# Revit family: DSP_A3-1-External-Lourve-Metal-Door-Full-Louvre-Single
name_source: partatom
category: Doors
revit_build: Autodesk Revit 2016 (Build: 20150220_1215(x64)
units: mm (PartAtom-declared; Revit-internal decimal feet)

## family parameters
Always vertical = Yes
Cut with Voids When Loaded = No
Host = Wall
Room Calculation Point = No
Shared = No

## types (1)
- 914 x 2438mm Louvre
    Cavity Closer Depth = 85 mm  [stored 0.278871 ft]
    Cavity Closer Offset from Ext = 102.5 mm  [stored 0.336286 ft]
    Cavity Closer Width = 50 mm  [stored 0.164042 ft]
    Cill Extension = 25 mm  [stored 0.082021 ft]
    Cill Projection = 30 mm  [stored 0.0984252 ft]
    Cill Thickness = 54.5 mm  [stored 0.178806 ft]
    Construction Type = SF-03
    DONT CHANGE Louvre Length = 722 mm
    Door Panel Height = 2328 mm
    Door Panel Thickness = 44 mm  [stored 0.144357 ft]
    Door Panel Width = 947 mm
    FrameDepth = 89 mm  [stored 0.291995 ft]
    FrameOffset - External = 25 mm  [stored 0.082021 ft]
    FrameWidth = 42 mm  [stored 0.137795 ft]
    Function = Interior
    Handle Style = Handle Domestic (2)
    Handle X Distance = 75 mm  [stored 0.246063 ft]
    Handle Z Distance = 1050 mm  [stored 3.44488 ft]
    Height = 2438 mm
    Keynote = L20
    L Louvre to Handle = 541.5 mm  [stored 1.77657 ft]
    Lower Louvre Height = 300 mm
    Material Door = Metal - Aluminium - Dark
    Material Frame = Metal - Aluminium - Dark
    Material Ironmongery = Door - Handle
    No of Louvres (Lower) = 6
    No of Louvres (Upper) = 44
    O/A Frame Width = 64 mm  [stored 0.209974 ft]
    Operation = DoubleDoorSingleSwing
    Rough Height = 2438 mm
    Rough Width = 2000 mm  [stored 6.56168 ft]
    Stile Bottom Rail = 150 mm
    Stile Hanging = 100 mm  [stored 0.328084 ft]
    Stile Lock Rail = 150 mm
    Stile Shutting = 125 mm  [stored 0.410105 ft]
    Stile Top Rail = 150 mm
    Structural Tolerance = 6.5 mm
    Thickness = 44 mm  [stored 0.144357 ft]
    Tolerance = 3 mm  [stored 0.00984252 ft]
    Top Louvre Height = 2025 mm  [stored 6.6437 ft]
    Undercut = 4 mm  [stored 0.0131234 ft]
    Vis - Cavity Closers = Yes
    Vis - Ironmongery = Yes
    Wall Closure = By host
    Width = 2000 mm  [stored 6.56168 ft]
    Wrap Layers (Ext) from Ext = 102.5 mm  [stored 0.336286 ft]
    Wrap Layers (Int) from Ext = 177.5 mm

note: [stored X ft] marks values corroborated as IEEE doubles in the binary element streams (Revit-internal decimal feet)

## geometry (parser evidence)
native form markers: Sweep x5
no freeform markers — native parametric forms only
